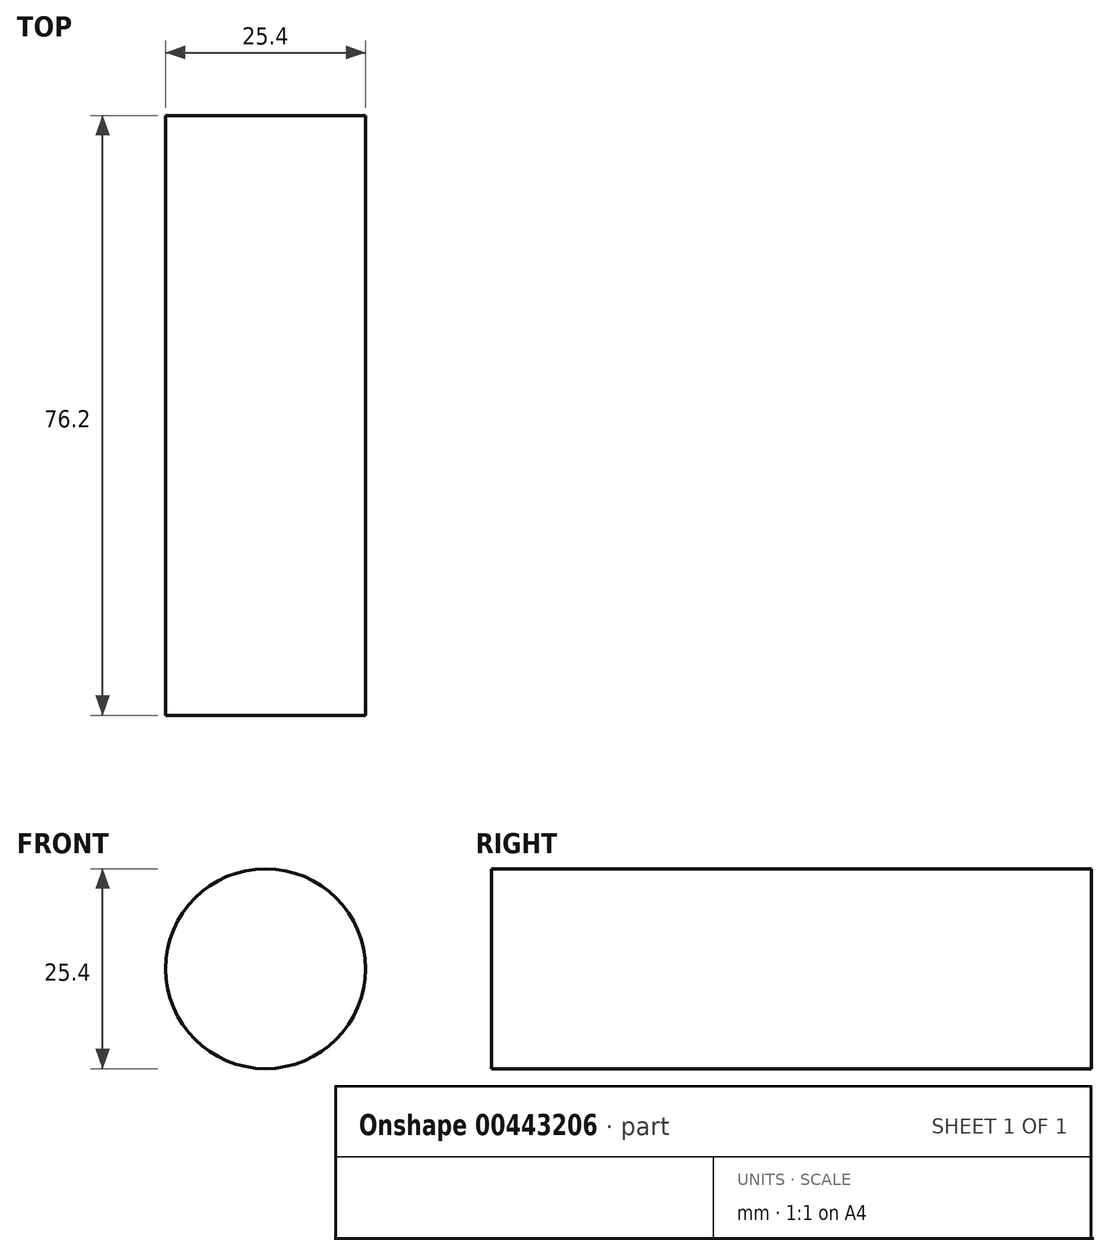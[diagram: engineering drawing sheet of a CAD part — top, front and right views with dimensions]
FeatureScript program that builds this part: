
annotation { "Feature Type Name" : "Feature", "Feature Type Description" : "" }
export const myFeature = defineFeature(function(context is Context, id is Id, definition is map)
    precondition{}
    {
        {
            var Q0;
            Q0=qCreatedBy(makeId("Front.planeOp"),FACE);
            var sketch = newSketch(context, id + "F0", { "sketchPlane" : qUnion([Q0])});
            skCircle(sketch, "E0", {"center": v(-41.91, 42.96) * mm, "radius": 12.7 * mm});
            skSolve(sketch);
        }
        {
            var Q0;
            Q0 = qSketchRegion(id + "F0", true);
            extrude(context, id + "F1", {"entities" : qUnion([Q0]), "depth" : 76.2 * mm});
        }
    });
